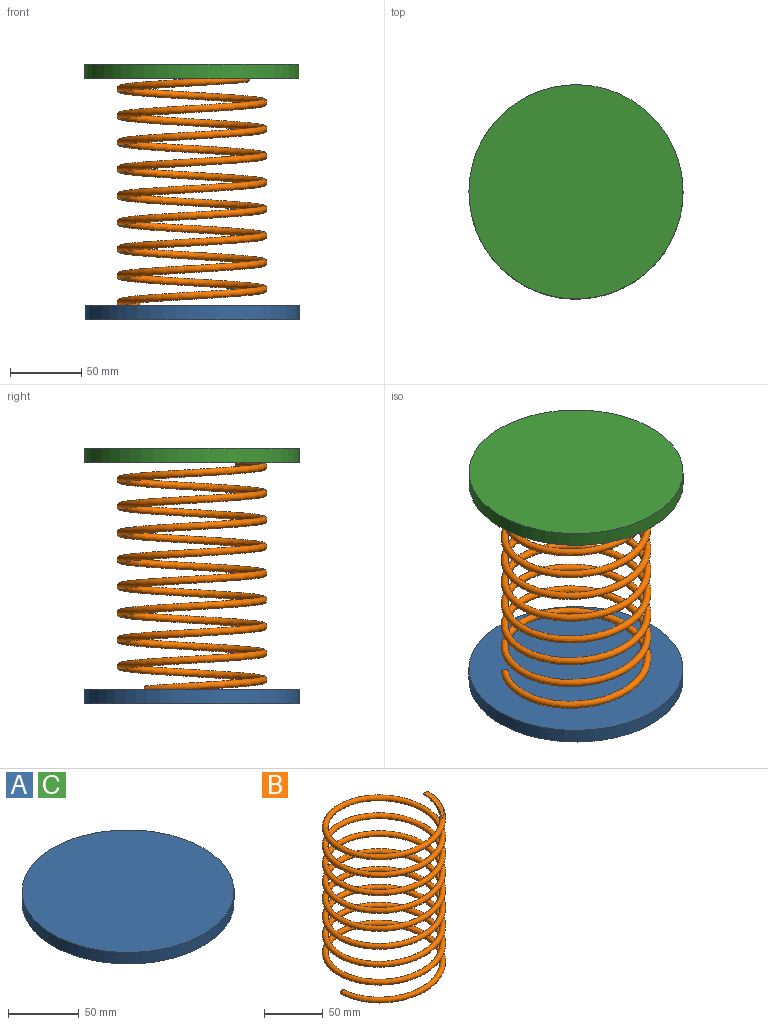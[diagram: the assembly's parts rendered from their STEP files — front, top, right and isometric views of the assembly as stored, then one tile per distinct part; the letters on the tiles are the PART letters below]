
ASSEMBLY  parts=3 mates=4
PART A: 3 faces, bbox 150x150x10 mm
  f0: cylinder r=75mm len=150mm, axis (0,0,1), area 4712.4mm2, adj f1,f2
  f1: plane 150x150mm, normal (0,0,-1), area 17671.5mm2, adj f0
  f2: plane 150x150mm, normal (0,0,1), area 17671.5mm2, adj f0
PART B: 5 faces, bbox 105x110.4x170.6 mm
  f0: bspline ~170.59x110.4mm, area 41553.7mm2, adj f1,f2,f3,f4
  f1: plane 5x2.5mm, normal (0,1,0), area 9.8mm2, adj f0,f4
  f2: plane 5x2.5mm, normal (0,1,0), area 9.8mm2, adj f0,f3
  f3: plane 37.38x19.27mm, normal (0,0,1), area 187.1mm2, adj f0,f2
  f4: plane 37.38x19.27mm, normal (0,0,-1), area 184.9mm2, adj f0,f1
PART C: same geometry as A
PLACE A at identity
PLACE B rot(axis=(0,0,-1),39.8deg) t=(0,0,0)mm
PLACE C rot(axis=(0,0,1),3.3deg) t=(0,0,168.73)mm
MATE cylindrical C.f0 <-> A.f0  axis (0,0,1) through (0,0,163.73)mm
MATE cylindrical B.f4 <-> A.f0  axis (0,0,1) through (0,0,0)mm
MATE planar B.f3 <-> C.f0  axis (0,0,1) through (36.51,-30.38,158.73)mm
MATE planar B.f4 <-> A.f0  axis (0,0,1) through (-50.37,-5.81,0)mm
